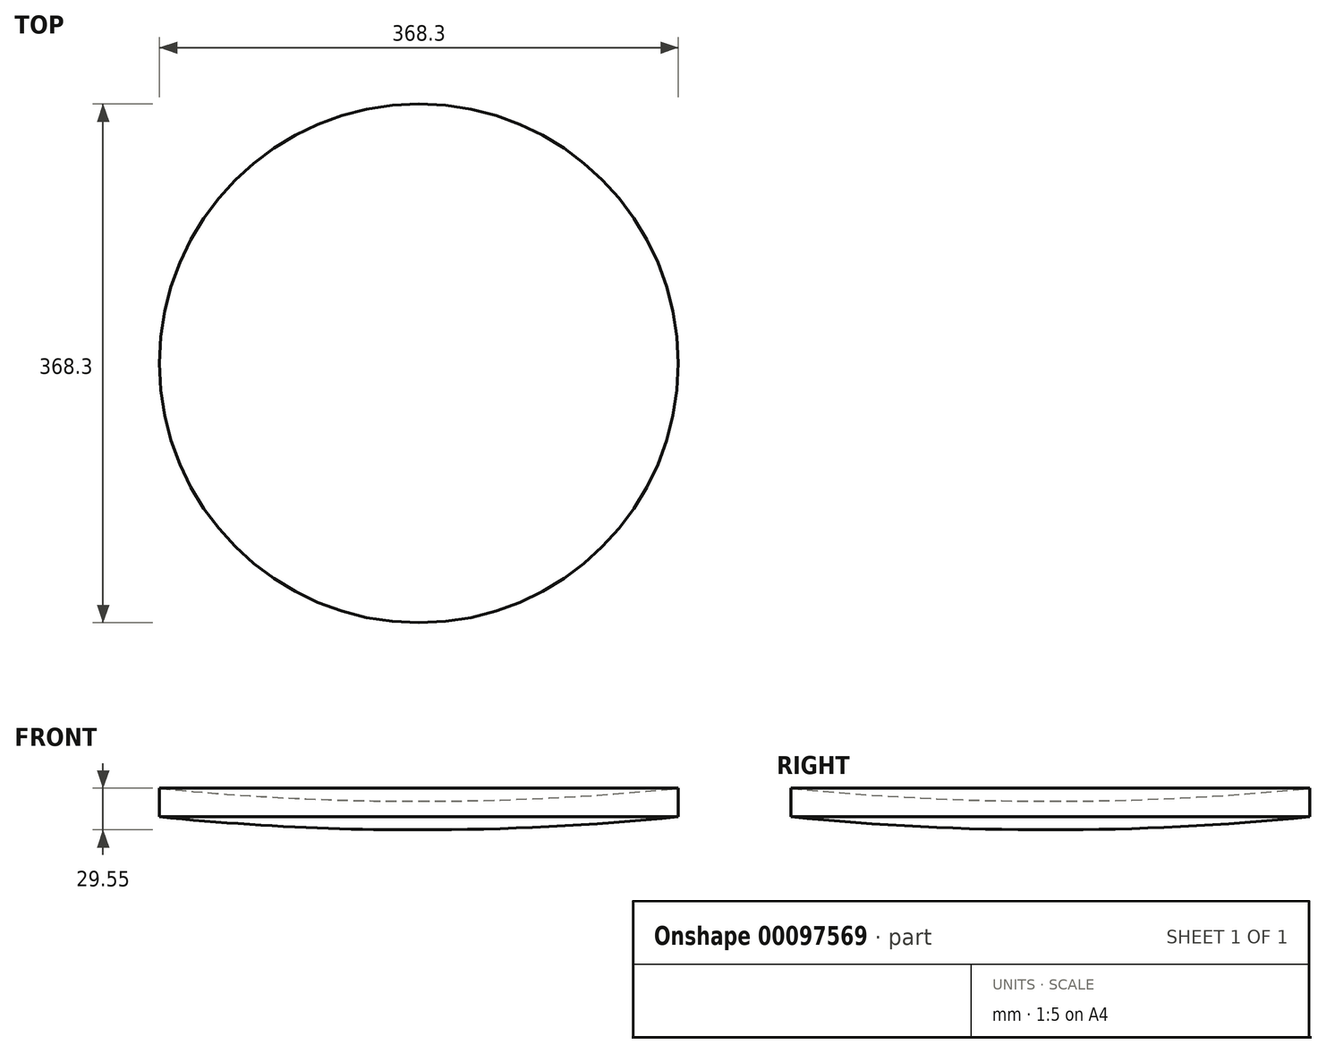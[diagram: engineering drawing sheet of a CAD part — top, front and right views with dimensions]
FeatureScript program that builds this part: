
annotation { "Feature Type Name" : "Feature", "Feature Type Description" : "" }
export const myFeature = defineFeature(function(context is Context, id is Id, definition is map)
    precondition{}
    {
        {
            var Q0;
            Q0=qCreatedBy(makeId("Front.planeOp"),FACE);
            var sketch = newSketch(context, id + "F0", { "sketchPlane" : qUnion([Q0])});
            skLineSegment(sketch, "E0.left", {"start": v(-184.15, 10.16) * mm, "end": v(-184.15, -10.16) * mm});
            skLineSegment(sketch, "E0.right", {"start": v(184.15, 10.16) * mm, "end": v(184.15, -10.16) * mm});
            skPoint(sketch, "E0.middle", {"position": v(0, 0) * mm});
            skArc(sketch, "E1", {"start": v(-184.15, -10.16) * mm, "mid": v(-92.2, -17.08) * mm, "end": v(0, -19.4) * mm});
            skArc(sketch, "E2", {"start": v(-184.15, 10.16) * mm, "mid": v(-92.2, 3.24) * mm, "end": v(0, 0.93) * mm});
            skLineSegment(sketch, "E3", {"start": v(0, 0) * mm, "end": v(0, 44.65) * mm, "construction": true});
            skPoint(sketch, "E3.endSnap0", {"position": v(0, 0.93) * mm});
            skLineSegment(sketch, "E4", {"start": v(0, -19.4) * mm, "end": v(0, 0.93) * mm});
            skSolve(sketch);
        }
        {
            var Q0;
            Q0=makeQuery(id+"F0.imprint","IMPRINT",FACE,{"disambiguationData":[TD([[makeQuery(id+"F0.imprint","IMPRINT",EDGE,{"derivedFrom":sQuery(id+"F0.wireOp",EDGE,"E0.left")}),1.0]])]});
            var Q1;
            Q1=sQuery(id+"F0.wireOp",EDGE,"E3");
            revolve(context, id + "F1", {"entities" : qUnion([Q0]), "axis" : qUnion([Q1]), "revolveType" : RevolveType.FULL});
        }
    });
